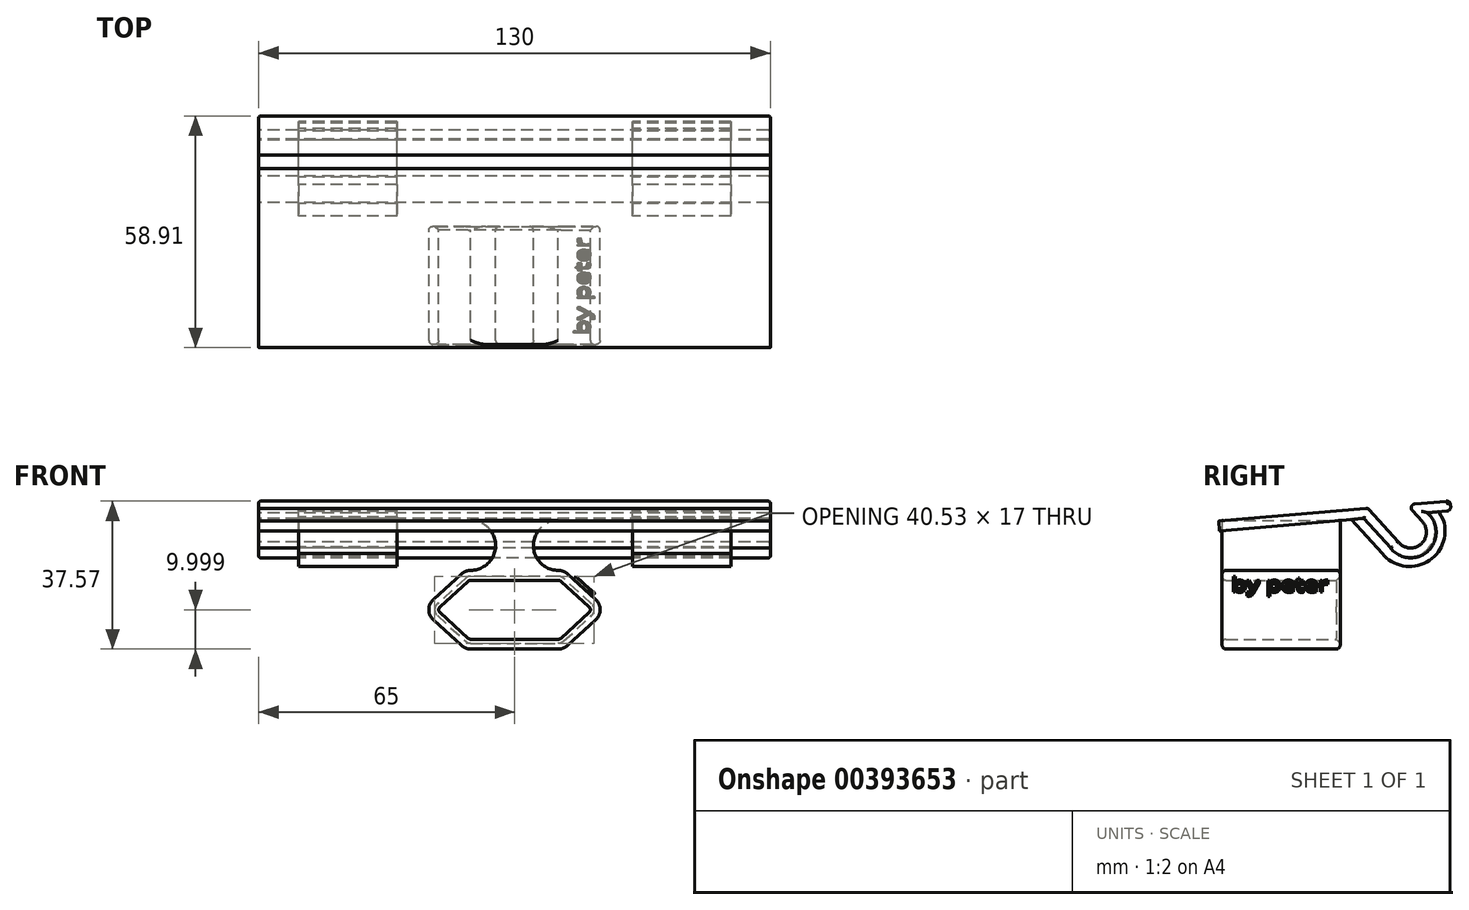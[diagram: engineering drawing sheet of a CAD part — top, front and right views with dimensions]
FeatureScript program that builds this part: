
annotation { "Feature Type Name" : "Feature", "Feature Type Description" : "" }
export const myFeature = defineFeature(function(context is Context, id is Id, definition is map)
    precondition{}
    {
        {
            var Q0;
            Q0=qCreatedBy(makeId("Right.planeOp"),FACE);
            var sketch = newSketch(context, id + "F0", { "sketchPlane" : qUnion([Q0])});
            skLineSegment(sketch, "E0", {"start": v(-30.98, 0) * mm, "end": v(7.02, 0) * mm});
            skLineSegment(sketch, "E1", {"start": v(17.02, 0) * mm, "end": v(28.02, 0) * mm});
            skLineSegment(sketch, "E2", {"start": v(7.02, 0) * mm, "end": v(13.96, -9.22) * mm});
            skLineSegment(sketch, "E3", {"start": v(17.02, 0) * mm, "end": v(20.52, -4.66) * mm});
            skArc(sketch, "E4", {"start": v(13.96, -9.22) * mm, "mid": v(19.61, -10.35) * mm, "end": v(20.52, -4.66) * mm});
            skLineSegment(sketch, "E5.0", {"start": v(21.96, -2.5) * mm, "end": v(28.02, -2.5) * mm});
            skArc(sketch, "E5.1", {"start": v(11.91, -10.65) * mm, "mid": v(21.42, -12.1) * mm, "end": v(21.96, -2.5) * mm});
            skLineSegment(sketch, "E5.2", {"start": v(5.77, -2.5) * mm, "end": v(11.91, -10.65) * mm});
            skLineSegment(sketch, "E5.3", {"start": v(-30.98, -2.5) * mm, "end": v(5.77, -2.5) * mm});
            skLineSegment(sketch, "E6", {"start": v(-30.98, 0) * mm, "end": v(-30.98, -2.5) * mm});
            skLineSegment(sketch, "E7", {"start": v(28.02, 0) * mm, "end": v(28.02, -2.5) * mm});
            skLineSegment(sketch, "E8.0", {"start": v(26.09, -5) * mm, "end": v(28.02, -5) * mm});
            skArc(sketch, "E8.1", {"start": v(9.87, -12.1) * mm, "mid": v(20.94, -15.3) * mm, "end": v(26.09, -5) * mm});
            skLineSegment(sketch, "E8.2", {"start": v(3.02, -3) * mm, "end": v(9.87, -12.1) * mm});
            skSolve(sketch);
        }
        {
            var Q0;
            Q0 = qSketchRegion(id + "F0", true);
            extrude(context, id + "F1", {"entities" : qUnion([Q0]), "endBound" : BoundingType.SYMMETRIC, "depth" : 130 * mm});
        }
        {
            var Q0;
            Q0=makeQuery(id+"F1.opExtrude","SWEPT_EDGE",EDGE,{"disambiguationData":[OSD([sQuery(id+"F0.wireOp",EDGE,"E1"),sQuery(id+"F0.wireOp",EDGE,"E7")])]});
            fillet(context, id + "F2", {"entities" : qUnion([Q0]), "radius" : 1 * mm, "tangentPropagation" : true, "rho" : 0.5, "crossSection" : FilletCrossSection.CONIC, "allowEdgeOverflow" : false});
        }
        {
            var Q0;
            Q0=makeQuery(id+"F1.opExtrude","SWEPT_EDGE",EDGE,{"disambiguationData":[OSD([sQuery(id+"F0.wireOp",EDGE,"E5.0"),sQuery(id+"F0.wireOp",EDGE,"E7")])]});
            fillet(context, id + "F3", {"entities" : qUnion([Q0]), "radius" : 1 * mm, "tangentPropagation" : true, "allowEdgeOverflow" : false});
        }
        {
            var Q0;
            Q0=makeQuery(id+"F1.opExtrude","SWEPT_EDGE",EDGE,{"disambiguationData":[OSD([sQuery(id+"F0.wireOp",EDGE,"E1"),sQuery(id+"F0.wireOp",EDGE,"E3")])]});
            fillet(context, id + "F4", {"entities" : qUnion([Q0]), "radius" : 1 * mm, "tangentPropagation" : true, "allowEdgeOverflow" : false});
        }
        {
            var Q0;
            Q0=makeQuery(id+"F1.opExtrude","SWEPT_EDGE",EDGE,{"disambiguationData":[OSD([sQuery(id+"F0.wireOp",EDGE,"E0"),sQuery(id+"F0.wireOp",EDGE,"E2")])]});
            fillet(context, id + "F5", {"entities" : qUnion([Q0]), "radius" : 1 * mm, "tangentPropagation" : true, "allowEdgeOverflow" : false});
        }
        {
            var Q0;
            Q0=makeQuery(id+"F1.opExtrude","CAP_EDGE",EDGE,{"disambiguationData":[OSD([sQuery(id+"F0.wireOp",EDGE,"E2")])],"isStart":false});
            var Q1;
            Q1=makeQuery(id+"F1.opExtrude","CAP_EDGE",EDGE,{"disambiguationData":[OSD([sQuery(id+"F0.wireOp",EDGE,"E3")])],"isStart":false});
            var Q2;
            Q2=makeQuery(id+"F1.opExtrude","CAP_EDGE",EDGE,{"disambiguationData":[OSD([sQuery(id+"F0.wireOp",EDGE,"E5.1")])],"isStart":false});
            var Q3;
            Q3=makeQuery(id+"F1.opExtrude","CAP_EDGE",EDGE,{"disambiguationData":[OSD([sQuery(id+"F0.wireOp",EDGE,"E5.3")])],"isStart":false});
            fillet(context, id + "F6", {"entities" : qUnion([Q0, Q1, Q2, Q3]), "radius" : .5 * mm, "tangentPropagation" : true, "allowEdgeOverflow" : false});
        }
        {
            var Q0;
            Q0=makeQuery(id+"F1.opExtrude","CAP_EDGE",EDGE,{"disambiguationData":[OSD([sQuery(id+"F0.wireOp",EDGE,"E0")])],"isStart":true});
            var Q1;
            Q1=makeQuery(id+"F1.opExtrude","CAP_EDGE",EDGE,{"disambiguationData":[OSD([sQuery(id+"F0.wireOp",EDGE,"E5.0")])],"isStart":true});
            var Q2;
            Q2=makeQuery(id+"F1.opExtrude","CAP_EDGE",EDGE,{"disambiguationData":[OSD([sQuery(id+"F0.wireOp",EDGE,"E5.1")])],"isStart":true});
            var Q3;
            Q3=makeQuery(id+"F1.opExtrude","CAP_EDGE",EDGE,{"disambiguationData":[OSD([sQuery(id+"F0.wireOp",EDGE,"E5.3")])],"isStart":true});
            fillet(context, id + "F7", {"entities" : qUnion([Q0, Q1, Q2, Q3]), "radius" : .5 * mm, "tangentPropagation" : true, "allowEdgeOverflow" : false});
        }
        {
            var Q0;
            Q0=makeQuery(id+"F1.opExtrude","SWEPT_BODY",BODY,{"disambiguationData":[OSD([sQuery(id+"F0.wireOp",EDGE,"E0"),sQuery(id+"F0.wireOp",EDGE,"E1"),sQuery(id+"F0.wireOp",EDGE,"E2"),sQuery(id+"F0.wireOp",EDGE,"E3"),sQuery(id+"F0.wireOp",EDGE,"E4"),sQuery(id+"F0.wireOp",EDGE,"E5.0"),sQuery(id+"F0.wireOp",EDGE,"E5.1"),sQuery(id+"F0.wireOp",EDGE,"E5.2"),sQuery(id+"F0.wireOp",EDGE,"E5.3"),sQuery(id+"F0.wireOp",EDGE,"E6"),sQuery(id+"F0.wireOp",EDGE,"E7")])]});
            var Q1;
            {var subQ0=sQuery(id+"F0.wireOp",EDGE,"E0");Q1=makeQuery(id+"F5.opFillet","BLEND_EDGE",EDGE,{"blendedFrom":[makeQuery(id+"F1.opExtrude","SWEPT_EDGE",EDGE,{"disambiguationData":[OSD([subQ0,sQuery(id+"F0.wireOp",EDGE,"E2")])]}),makeQuery(id+"F1.opExtrude","SWEPT_FACE",FACE,{"disambiguationData":[OSD([subQ0])]})],"blendedInto":[makeQuery(id+"F1.opExtrude","SWEPT_FACE",FACE,{"disambiguationData":[OSD([subQ0])]})]});}
            transform(context, id + "F8", {"entities" : qUnion([Q0]), "transformType" : TransformType.ROTATION, "transformAxis" : qUnion([Q1]), "angle" : 5 * degree, "oppositeDirection" : true, "makeCopy" : false});
        }
        {
            var Q0;
            Q0=makeQuery(id+"F1.opExtrude","SWEPT_BODY",BODY,{"disambiguationData":[OSD([sQuery(id+"F0.wireOp",EDGE,"E0"),sQuery(id+"F0.wireOp",EDGE,"E1"),sQuery(id+"F0.wireOp",EDGE,"E2"),sQuery(id+"F0.wireOp",EDGE,"E3"),sQuery(id+"F0.wireOp",EDGE,"E4"),sQuery(id+"F0.wireOp",EDGE,"E5.0"),sQuery(id+"F0.wireOp",EDGE,"E5.1"),sQuery(id+"F0.wireOp",EDGE,"E5.2"),sQuery(id+"F0.wireOp",EDGE,"E5.3"),sQuery(id+"F0.wireOp",EDGE,"E6"),sQuery(id+"F0.wireOp",EDGE,"E7")])]});
            transform(context, id + "F9", {"entities" : qUnion([Q0]), "transformType" : TransformType.TRANSLATION_3D, "dx" : 0 * mm, "dy" : 0 * mm, "dz" : 3.15 * mm, "makeCopy" : false});
        }
        {
            var Q0;
            Q0=qCreatedBy(makeId("Front.planeOp"),FACE);
            var sketch = newSketch(context, id + "F10", { "sketchPlane" : qUnion([Q0])});
            skLineSegment(sketch, "E9", {"start": v(-31.41, -22.63) * mm, "end": v(31.46, -22.63) * mm, "construction": true});
            skLineSegment(sketch, "E10", {"start": v(-30.23, -15.13) * mm, "end": v(27.4, -15.13) * mm, "construction": true});
            skLineSegment(sketch, "E11", {"start": v(-30.68, -30.13) * mm, "end": v(29.88, -30.13) * mm, "construction": true});
            skLineSegment(sketch, "E12", {"start": v(0, -37.5) * mm, "end": v(0, -9.98) * mm, "construction": true});
            skLineSegment(sketch, "E13", {"start": v(-11.5, -37.53) * mm, "end": v(-11.5, -9.13) * mm, "construction": true});
            skLineSegment(sketch, "E14", {"start": v(11.5, -37.58) * mm, "end": v(11.5, -9.47) * mm, "construction": true});
            skLineSegment(sketch, "E15", {"start": v(19.75, -36.26) * mm, "end": v(19.75, -8.88) * mm, "construction": true});
            skLineSegment(sketch, "E16", {"start": v(-19.75, -36.85) * mm, "end": v(-19.75, -7.26) * mm, "construction": true});
            skPoint(sketch, "E17", {"position": v(-11.5, -30.13) * mm});
            skPoint(sketch, "E18", {"position": v(11.5, -30.13) * mm});
            skPoint(sketch, "E19", {"position": v(19.75, -22.63) * mm});
            skPoint(sketch, "E20", {"position": v(11.5, -15.13) * mm});
            skPoint(sketch, "E21", {"position": v(-11.5, -15.13) * mm});
            skPoint(sketch, "E22", {"position": v(-19.75, -22.63) * mm});
            skSolve(sketch);
        }
        {
            var Q0;
            Q0=qCreatedBy(makeId("Front.planeOp"),FACE);
            var sketch = newSketch(context, id + "F11", { "sketchPlane" : qUnion([Q0])});
            skLineSegment(sketch, "E23", {"start": v(-18.94, -23.37) * mm, "end": v(-11.79, -29.87) * mm});
            skLineSegment(sketch, "E24", {"start": v(-11.11, -30.13) * mm, "end": v(11.11, -30.13) * mm});
            skLineSegment(sketch, "E25", {"start": v(11.79, -29.87) * mm, "end": v(18.94, -23.37) * mm});
            skLineSegment(sketch, "E26", {"start": v(18.94, -21.9) * mm, "end": v(11.79, -15.4) * mm});
            skLineSegment(sketch, "E27", {"start": v(11.11, -15.13) * mm, "end": v(-11.11, -15.13) * mm});
            skLineSegment(sketch, "E28", {"start": v(-11.79, -15.4) * mm, "end": v(-18.94, -21.9) * mm});
            skPoint(sketch, "E29.visualSharp", {"position": v(-19.75, -22.63) * mm});
            skArc(sketch, "E29.filletArc", {"start": v(-18.94, -21.9) * mm, "mid": v(-19.26, -22.63) * mm, "end": v(-18.94, -23.37) * mm});
            skPoint(sketch, "E30.visualSharp", {"position": v(-11.5, -15.13) * mm});
            skArc(sketch, "E30.filletArc", {"start": v(-11.11, -15.13) * mm, "mid": v(-11.47, -15.2) * mm, "end": v(-11.79, -15.4) * mm});
            skPoint(sketch, "E31.visualSharp", {"position": v(11.5, -15.13) * mm});
            skArc(sketch, "E31.filletArc", {"start": v(11.79, -15.4) * mm, "mid": v(11.47, -15.2) * mm, "end": v(11.11, -15.13) * mm});
            skPoint(sketch, "E32.visualSharp", {"position": v(19.75, -22.63) * mm});
            skArc(sketch, "E32.filletArc", {"start": v(18.94, -23.37) * mm, "mid": v(19.26, -22.63) * mm, "end": v(18.94, -21.9) * mm});
            skPoint(sketch, "E33.visualSharp", {"position": v(11.5, -30.13) * mm});
            skArc(sketch, "E33.filletArc", {"start": v(11.11, -30.13) * mm, "mid": v(11.47, -30.06) * mm, "end": v(11.79, -29.87) * mm});
            skPoint(sketch, "E34.visualSharp", {"position": v(-11.5, -30.13) * mm});
            skArc(sketch, "E34.filletArc", {"start": v(-11.79, -29.87) * mm, "mid": v(-11.47, -30.06) * mm, "end": v(-11.11, -30.13) * mm});
            skArc(sketch, "E35.0", {"start": v(-13.47, -31.72) * mm, "mid": v(-12.38, -32.4) * mm, "end": v(-11.11, -32.63) * mm});
            skLineSegment(sketch, "E35.1", {"start": v(20.62, -20.04) * mm, "end": v(13.47, -13.54) * mm});
            skArc(sketch, "E35.2", {"start": v(20.62, -25.22) * mm, "mid": v(21.76, -22.63) * mm, "end": v(20.62, -20.04) * mm});
            skLineSegment(sketch, "E35.3", {"start": v(13.47, -31.72) * mm, "end": v(20.62, -25.22) * mm});
            skArc(sketch, "E35.4", {"start": v(11.11, -32.63) * mm, "mid": v(12.38, -32.4) * mm, "end": v(13.47, -31.72) * mm});
            skArc(sketch, "E35.5", {"start": v(13.47, -13.54) * mm, "mid": v(12.38, -12.87) * mm, "end": v(11.11, -12.63) * mm});
            skLineSegment(sketch, "E35.6", {"start": v(-11.11, -32.63) * mm, "end": v(11.11, -32.63) * mm});
            skLineSegment(sketch, "E35.7", {"start": v(11.11, -12.63) * mm, "end": v(-11.11, -12.63) * mm});
            skArc(sketch, "E35.8", {"start": v(-11.11, -12.63) * mm, "mid": v(-12.38, -12.87) * mm, "end": v(-13.47, -13.54) * mm});
            skLineSegment(sketch, "E35.9", {"start": v(-13.47, -13.54) * mm, "end": v(-20.62, -20.04) * mm});
            skArc(sketch, "E35.10", {"start": v(-20.62, -20.04) * mm, "mid": v(-21.76, -22.63) * mm, "end": v(-20.62, -25.22) * mm});
            skLineSegment(sketch, "E35.11", {"start": v(-20.62, -25.22) * mm, "end": v(-13.47, -31.72) * mm});
            skArc(sketch, "E36", {"start": v(-11.11, -12.63) * mm, "mid": v(-4.8, -6.32) * mm, "end": v(-11.11, 0) * mm});
            skArc(sketch, "E37", {"start": v(11.11, 0) * mm, "mid": v(4.8, -6.32) * mm, "end": v(11.11, -12.63) * mm});
            skLineSegment(sketch, "E38", {"start": v(-11.11, 0) * mm, "end": v(11.11, 0) * mm});
            skSolve(sketch);
        }
        {
            var Q0;
            Q0 = qSketchRegion(id + "F11", true);
            extrude(context, id + "F12", {"entities" : qUnion([Q0]), "depth" : 30 * mm, "hasSecondDirection" : true, "secondDirectionOppositeDirection" : false, "secondDirectionDepth" : 0 * mm});
        }
        {
            var Q0;
            Q0=makeQuery(id+"F12.opExtrude","CAP_EDGE",EDGE,{"disambiguationData":[OSD([sQuery(id+"F11.wireOp",EDGE,"E37")])],"isStart":false});
            fillet(context, id + "F13", {"entities" : qUnion([Q0]), "radius" : 1 * mm, "tangentPropagation" : true, "allowEdgeOverflow" : false});
        }
        {
            var Q0;
            Q0=makeQuery(id+"F12.opExtrude","CAP_EDGE",EDGE,{"disambiguationData":[OSD([sQuery(id+"F11.wireOp",EDGE,"E27")])],"isStart":false});
            fillet(context, id + "F14", {"entities" : qUnion([Q0]), "radius" : 1 * mm, "tangentPropagation" : true, "allowEdgeOverflow" : false});
        }
        {
            var Q0;
            Q0=makeQuery(id+"F12.opExtrude","CAP_EDGE",EDGE,{"disambiguationData":[OSD([sQuery(id+"F11.wireOp",EDGE,"E35.9")])],"isStart":true});
            var Q1;
            Q1=makeQuery(id+"F12.opExtrude","CAP_EDGE",EDGE,{"disambiguationData":[OSD([sQuery(id+"F11.wireOp",EDGE,"E35.8")])],"isStart":true});
            fillet(context, id + "F15", {"entities" : qUnion([Q0, Q1]), "radius" : 1 * mm, "tangentPropagation" : true, "allowEdgeOverflow" : false});
        }
        {
            var Q0;
            Q0=makeQuery(id+"F12.opExtrude","CAP_EDGE",EDGE,{"disambiguationData":[OSD([sQuery(id+"F11.wireOp",EDGE,"E27")])],"isStart":true});
            chamfer(context, id + "F16", {"entities" : qUnion([Q0]), "width" : 1 * mm, "tangentPropagation" : true});
        }
        {
            var Q0;
            Q0=makeQuery(id+"F12.opExtrude","SWEPT_FACE",FACE,{"disambiguationData":[OSD([sQuery(id+"F11.wireOp",EDGE,"E35.1")])]});
            var sketch = newSketch(context, id + "F17", { "sketchPlane" : qUnion([Q0])});
            skText(sketch, "E39", { "text": "by peter", "fontName": "OpenSans-Regular.ttf"});
            const initialGuessF17  = {"E39": [0.02596, -0.02767, 0, 1, 0.00459]};
            skSetInitialGuess(sketch, initialGuessF17);
            skSolve(sketch);
        }
        {
            var Q0;
            Q0 = qSketchRegion(id + "F17", true);
            extrude(context, id + "F18", {"entities" : qUnion([Q0]), "operationType" : NewBodyOperationType.ADD, "depth" : 1 * mm});
        }
        {
            var Q0;
            Q0=qCreatedBy(makeId("Right.planeOp"),FACE);
            var sketch = newSketch(context, id + "F19", { "sketchPlane" : qUnion([Q0])});
            skLineSegment(sketch, "E40.0", {"start": v(21.96, -2.5) * mm, "end": v(24.99, -2.5) * mm});
            skArc(sketch, "E40.1", {"start": v(11.91, -10.65) * mm, "mid": v(21.42, -12.1) * mm, "end": v(21.96, -2.5) * mm});
            skLineSegment(sketch, "E40.2", {"start": v(5.77, -2.5) * mm, "end": v(11.91, -10.65) * mm});
            skLineSegment(sketch, "E40.3", {"start": v(2.64, -2.5) * mm, "end": v(5.77, -2.5) * mm});
            skArc(sketch, "E41.1", {"start": v(9.87, -12.1) * mm, "mid": v(20.94, -15.3) * mm, "end": v(26.09, -5) * mm});
            skLineSegment(sketch, "E41.2", {"start": v(3.02, -3) * mm, "end": v(9.87, -12.1) * mm});
            skLineSegment(sketch, "E42", {"start": v(3.02, -3) * mm, "end": v(2.64, -2.5) * mm});
            skLineSegment(sketch, "E43", {"start": v(26.09, -5) * mm, "end": v(24.99, -2.5) * mm});
            skPoint(sketch, "E44.end.orphan", {"position": v(28.02, -2.5) * mm});
            skPoint(sketch, "E45.end.orphan", {"position": v(28.02, 0) * mm});
            skPoint(sketch, "E46.start.orphan", {"position": v(17.02, 0) * mm});
            skPoint(sketch, "E47.end.orphan", {"position": v(7.02, 0) * mm});
            skPoint(sketch, "E48.start.orphan", {"position": v(-30.98, 0) * mm});
            skSolve(sketch);
        }
        {
            var Q0;
            Q0 = qSketchRegion(id + "F19", true);
            var Q1;
            {var subQ1=sQuery(id+"F19.wireOp",EDGE,"E40.2");Q1=makeQuery(id+"F19.imprint","IMPRINT",FACE,{"disambiguationData":[TD([[makeQuery(id+"F19.imprint","IMPRINT",EDGE,{"derivedFrom":subQ1}),-1.0]])]});}
            extrude(context, id + "F20", {"entities" : qUnion([Q0, Q1]), "depth" : 25 * mm});
        }
        {
            var Q0;
            Q0=makeQuery(id+"F20.opExtrude","SWEPT_BODY",BODY,{"disambiguationData":[OSD([sQuery(id+"F19.wireOp",EDGE,"E40.0"),sQuery(id+"F19.wireOp",EDGE,"E40.1"),sQuery(id+"F19.wireOp",EDGE,"E40.2"),sQuery(id+"F19.wireOp",EDGE,"E40.3"),sQuery(id+"F19.wireOp",EDGE,"E41.1"),sQuery(id+"F19.wireOp",EDGE,"E41.2"),sQuery(id+"F19.wireOp",EDGE,"E42"),sQuery(id+"F19.wireOp",EDGE,"E43")])]});
            var Q1;
            {var subQ0=sQuery(id+"F0.wireOp",EDGE,"E2");Q1=makeQuery(id+"F5.opFillet","BLEND_EDGE",EDGE,{"blendedFrom":[makeQuery(id+"F1.opExtrude","SWEPT_EDGE",EDGE,{"disambiguationData":[OSD([sQuery(id+"F0.wireOp",EDGE,"E0"),subQ0])]}),makeQuery(id+"F1.opExtrude","SWEPT_FACE",FACE,{"disambiguationData":[OSD([subQ0])]})],"blendedInto":[makeQuery(id+"F1.opExtrude","SWEPT_FACE",FACE,{"disambiguationData":[OSD([subQ0])]})]});}
            transform(context, id + "F21", {"entities" : qUnion([Q0]), "transformType" : TransformType.ROTATION, "transformAxis" : qUnion([Q1]), "angle" : 5 * degree, "oppositeDirection" : true, "makeCopy" : false});
        }
        {
            var Q0;
            Q0=makeQuery(id+"F20.opExtrude","SWEPT_BODY",BODY,{"disambiguationData":[OSD([sQuery(id+"F19.wireOp",EDGE,"E40.0"),sQuery(id+"F19.wireOp",EDGE,"E40.1"),sQuery(id+"F19.wireOp",EDGE,"E40.2"),sQuery(id+"F19.wireOp",EDGE,"E40.3"),sQuery(id+"F19.wireOp",EDGE,"E41.1"),sQuery(id+"F19.wireOp",EDGE,"E41.2"),sQuery(id+"F19.wireOp",EDGE,"E42"),sQuery(id+"F19.wireOp",EDGE,"E43")])]});
            transform(context, id + "F22", {"entities" : qUnion([Q0]), "transformType" : TransformType.TRANSLATION_3D, "dx" : 0 * mm, "dy" : -0.5 * mm, "dz" : 3.5 * mm, "makeCopy" : false});
        }
        {
            var Q0;
            Q0=makeQuery(id+"F20.opExtrude","SWEPT_BODY",BODY,{"disambiguationData":[OSD([sQuery(id+"F19.wireOp",EDGE,"E40.0"),sQuery(id+"F19.wireOp",EDGE,"E40.1"),sQuery(id+"F19.wireOp",EDGE,"E40.2"),sQuery(id+"F19.wireOp",EDGE,"E40.3"),sQuery(id+"F19.wireOp",EDGE,"E41.1"),sQuery(id+"F19.wireOp",EDGE,"E41.2"),sQuery(id+"F19.wireOp",EDGE,"E42"),sQuery(id+"F19.wireOp",EDGE,"E43")])]});
            transform(context, id + "F23", {"entities" : qUnion([Q0]), "transformType" : TransformType.TRANSLATION_3D, "dx" : 30 * mm, "dy" : 0 * mm, "dz" : 0 * mm, "makeCopy" : false});
        }
        {
            var Q0;
            Q0=makeQuery(id+"F20.opExtrude","SWEPT_BODY",BODY,{"disambiguationData":[OSD([sQuery(id+"F19.wireOp",EDGE,"E40.0"),sQuery(id+"F19.wireOp",EDGE,"E40.1"),sQuery(id+"F19.wireOp",EDGE,"E40.2"),sQuery(id+"F19.wireOp",EDGE,"E40.3"),sQuery(id+"F19.wireOp",EDGE,"E41.1"),sQuery(id+"F19.wireOp",EDGE,"E41.2"),sQuery(id+"F19.wireOp",EDGE,"E42"),sQuery(id+"F19.wireOp",EDGE,"E43")])]});
            transform(context, id + "F24", {"entities" : qUnion([Q0]), "transformType" : TransformType.TRANSLATION_3D, "dx" : -84.9 * mm, "dy" : 0 * mm, "dz" : 0 * mm, "makeCopy" : true});
        }
    });
